# Revit family: PipeAccessories_Valve-Balancing_TA-Hydronics_STAD_DN10-50
name_source: partatom
category: Pipe Accessories
units: mm (PartAtom-declared; Revit-internal decimal feet)

## family parameters
Always vertical = Yes
Cut with Voids When Loaded = No
OmniClass Number = 23.65.55.14.17
OmniClass Title = Adjusting/Controlling Valves for Liquid Services
Part Type = Valve - Breaks Into
Round Connector Dimension = Use Diameter
Shared = No
Work Plane-Based = No

## types (1)
- TA-Hydronics_STAD_DN10-50
    BodyMaterial = TA-Hydronics_Ametal
    ConnectorDescription = DN 10-50: Female thread according to ISO 228. Thread length according to ISO 7/1.
    Description = Manual balancing valve
    HandleMaterial = TA-Hydronics_Polyamide
    Lookup Table Name = PipeAccessories_Valve-Balancing_TA-Hydronics_STAD_DN10-50
    Manufacturer = Tour&Andersson
    Max.WorkingTemperature = 120°C
    Min.WorkingTemperature = -20°C
    Model = STAD
    ModifiedIssue_ANZRS = 20141016.54 $
    Type Comments = Screwed ends
    URL = http://www.tahydronics.com

## geometry (parser evidence)
native form markers: Sweep x1
no freeform markers — native parametric forms only
